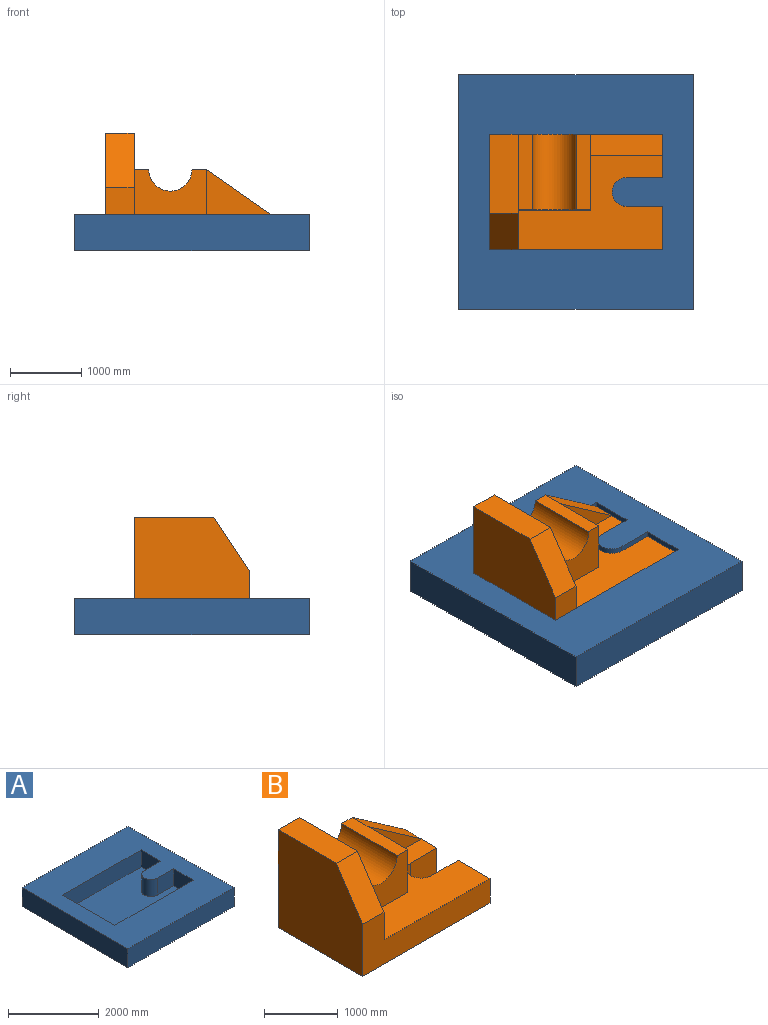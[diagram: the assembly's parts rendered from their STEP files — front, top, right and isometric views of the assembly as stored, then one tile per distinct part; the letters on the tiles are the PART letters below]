
ASSEMBLY  parts=2 mates=1
PART A: 15 faces, bbox 3302x3302x508 mm
  f0: plane 609.6x457.2mm, normal (-1,0,0), area 278709.1mm2, adj f1,f9,f11,f14
  f1: plane 2438.4x457.2mm, normal (0,1,0), area 1114836.5mm2, adj f0,f2,f9,f14
  f2: plane 1625.6x457.2mm, normal (1,0,0), area 743224.3mm2, adj f1,f3,f9,f14
  f3: plane 2438.4x457.2mm, normal (0,-1,0), area 1114836.5mm2, adj f2,f8,f9,f14
  f4: plane 3302x508mm, normal (0,-1,0), area 1677416mm2, adj f5,f7,f9,f10
  f5: plane 3302x508mm, normal (1,0,0), area 1677416mm2, adj f4,f6,f9,f10
  f6: plane 3302x508mm, normal (0,1,0), area 1677416mm2, adj f5,f7,f9,f10
  f7: plane 3302x508mm, normal (-1,0,0), area 1677416mm2, adj f4,f6,f9,f10
  f8: plane 609.6x457.2mm, normal (-1,0,0), area 278709.1mm2, adj f3,f9,f12,f14
  f9: plane 3302x3302mm, normal (0,0,1), area 7210650.7mm2, adj f0,f1,f2,f3,f4,f5,f6,f7
  f10: plane 3302x3302mm, normal (0,0,-1), area 10903204mm2, adj f4,f5,f6,f7
  f11: plane 508x457.2mm, normal (0,-1,0), area 232257.6mm2, adj f0,f9,f13,f14
  f12: plane 508x457.2mm, normal (0,1,0), area 232257.6mm2, adj f8,f9,f13,f14
  f13: cylinder r=203.2mm len=457.2mm, axis (0,0,-1), area 291863.5mm2, adj f9,f11,f12,f14
  f14: plane 2438.4x1625.6mm, normal (0,0,1), area 3692553.3mm2, adj f0,f1,f2,f3,f8,f11,f12,f13
PART B: 20 faces, bbox 2438.4x1625.6x1625.6 mm
  f0: plane 1066.8x203.2mm, normal (0,0,1), area 216773.8mm2, adj f1,f11,f15,f17
  f1: plane 1625.6x1219.2mm, normal (1,0,0), area 1029675.4mm2, adj f0,f4,f8,f11,f12,f15,f19
  f2: plane 508x406.4mm, normal (0,-1,0), area 206451.2mm2, adj f3,f7,f8,f9
  f3: plane 609.6x406.4mm, normal (1,0,0), area 247741.4mm2, adj f2,f8,f9,f11,f18
  f4: plane 2438.4x863.6mm, normal (0,-1,0), area 1176771.8mm2, adj f1,f5,f8,f9,f10,f19
  f5: plane 609.6x406.4mm, normal (1,0,0), area 247741.4mm2, adj f4,f6,f8,f9
  f6: plane 508x406.4mm, normal (0,1,0), area 206451.2mm2, adj f5,f7,f8,f9
  f7: cylinder r=203.2mm len=406.4mm, axis (0,0,-1), area 259434.2mm2, adj f2,f6,f8,f9
  f8: plane 2032x1320.8mm, normal (0,0,1), area 1638363.8mm2, adj f1,f2,f3,f4,f5,f6,f7,f13
  f9: plane 2438.4x1625.6mm, normal (0,0,-1), area 3692553.3mm2, adj f2,f3,f4,f5,f6,f7,f10,f11
  f10: plane 1625.6x1625.6mm, normal (-1,0,0), area 2449027.4mm2, adj f4,f9,f11,f12,f19
  f11: plane 2438.4x1625.6mm, normal (0,1,0), area 2424385.7mm2, adj f0,f1,f3,f9,f10,f12,f16,f17
  f12: plane 1117.6x406.4mm, normal (0,0,1), area 454192.6mm2, adj f1,f10,f11,f19
  f13: plane 1016x711.2mm, normal (0,-1,0), area 361289.6mm2, adj f8,f14,f18
  f14: plane 762x711.2mm, normal (1,0,0), area 541934.4mm2, adj f8,f13,f15,f16
  f15: plane 1016x711.2mm, normal (0,-1,0), area 576647.4mm2, adj f0,f1,f8,f14,f16,f17
  f16: plane 1066.8x203.2mm, normal (0,0,1), area 216773.8mm2, adj f11,f14,f15,f17,f18
  f17: cylinder r=304.8mm len=1066.8mm, axis (0,-1,0), area 1021522.3mm2, adj f0,f11,f15,f16
  f18: plane 1016x711.2mm, normal (0.57,0,0.82), area 378008.7mm2, adj f3,f11,f13,f16
  f19: plane 762x508mm, normal (0,-0.83,0.55), area 372185.2mm2, adj f1,f4,f10,f12
PLACE A t=(-667.48,143.63,-19.3)mm fixed
PLACE B t=(-667.48,143.63,6.1)mm
MATE slider B.f9 <-> A.f14  axis (0,0,-1) through (-732.42,143.63,6.1)mm
